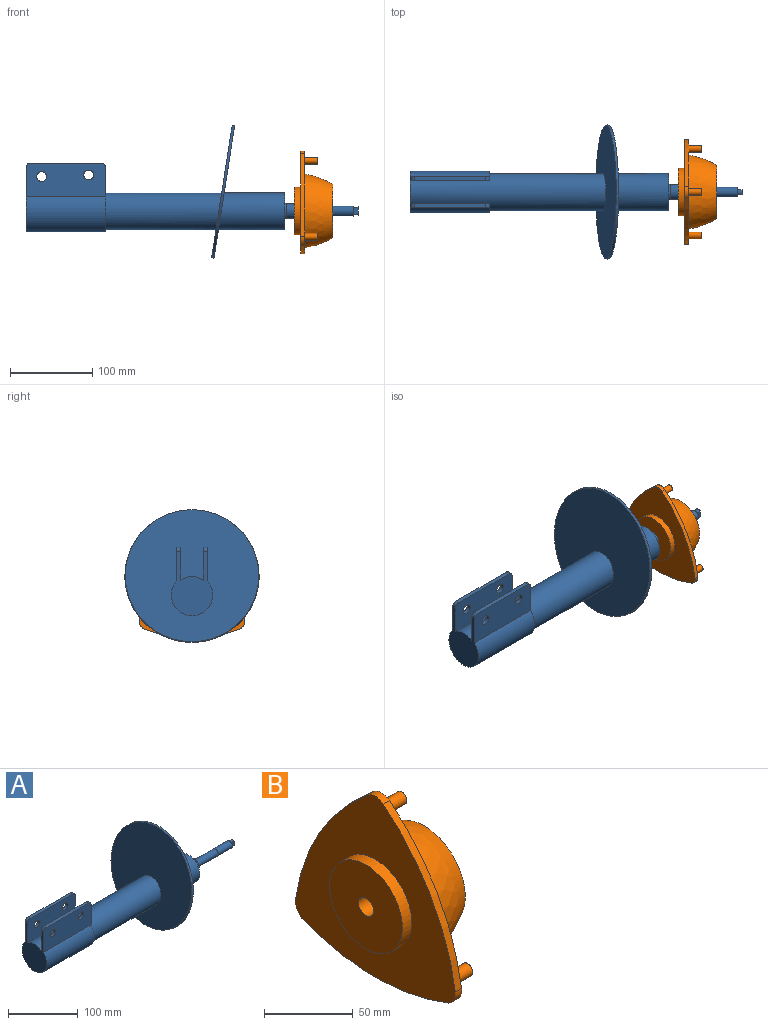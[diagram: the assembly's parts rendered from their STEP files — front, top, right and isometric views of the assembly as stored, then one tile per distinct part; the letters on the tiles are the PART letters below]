
ASSEMBLY  parts=2 mates=1
PART A: 41 faces, bbox 404x164.3x162.4 mm
  f0: plane 10x6mm, normal (1,0,0), area 56.2mm2, adj f1,f3,f12,f13
  f1: cylinder r=5mm len=6mm, axis (-1,0,0), area 38.6mm2, adj f0,f4,f12,f13
  f2: cylinder r=22.5mm len=80.19mm, axis (-1,0,0), area 10839.2mm2, adj f11,f15
  f3: cylinder r=5mm len=6mm, axis (-1,0,0), area 38.6mm2, adj f0,f4,f12,f13
  f4: plane 12x12mm, normal (1,0,0), area 56.9mm2, adj f1,f3,f5,f12,f13
  f5: cylinder r=6mm len=29mm, axis (-1,0,0), area 1093.3mm2, adj f4,f6
  f6: plane 12x12mm, normal (-1,0,0), area 3.7mm2, adj f5,f7
  f7: cylinder r=5.9mm len=42mm, axis (-1,0,0), area 1557mm2, adj f6,f8
  f8: plane 18x18mm, normal (1,0,0), area 145.1mm2, adj f7,f9
  f9: cylinder r=9mm len=18mm, axis (-1,0,0), area 565.5mm2, adj f8,f10
  f10: cone r=10mm half-angle=26.6deg, axis (-1,0,0), area 133.5mm2, adj f9,f11
  f11: plane 45x45mm, normal (1,0,0), area 1276.3mm2, adj f2,f10
  f12: plane 8x6mm, normal (0,1,0), area 48mm2, adj f0,f1,f3,f4
  f13: plane 8x6mm, normal (0,-1,0), area 48mm2, adj f0,f1,f3,f4
  f14: plane 161.94x160mm, normal (-0.99,0,0.15), area 18987.3mm2, adj f16,f26
  f15: plane 164.35x162.39mm, normal (0.99,0,-0.15), area 19223.6mm2, adj f2,f16
  f16: cone r=81.43mm half-angle=8.9deg, axis (0.99,0,-0.15), area 1530.6mm2, adj f14,f15
  f17: plane 86.5x5mm, normal (0,0,1), area 432.5mm2, adj f18,f24,f31,f32
  f18: plane 96.5x40.82mm, normal (0,1,0), area 3701.8mm2, adj f17,f19,f23,f25,f27,f28,f31,f32
  f19: cylinder r=25.25mm len=96.5mm, axis (-1,0,0), area 11302.8mm2, adj f18,f20,f23,f25
  f20: plane 96.5x40.82mm, normal (0,-1,0), area 3701.8mm2, adj f19,f21,f23,f25,f29,f30,f33,f34
  f21: plane 86.5x5mm, normal (0,0,1), area 432.5mm2, adj f20,f22,f33,f34
  f22: plane 96.5x40mm, normal (0,1,0), area 3623.1mm2, adj f21,f23,f25,f26,f29,f30,f33,f34
  f23: plane 78.25x50.5mm, normal (-1,0,0), area 2259.6mm2, adj f18,f19,f20,f22,f24,f26,f32,f34
  f24: plane 96.5x40mm, normal (0,-1,0), area 3623.1mm2, adj f17,f23,f25,f26,f27,f28,f31,f32
  f25: plane 78.25x50.5mm, normal (1,0,0), area 669.2mm2, adj f18,f19,f20,f22,f24,f26,f31,f33
  f26: cylinder r=22.5mm len=237.36mm, axis (-1,0,0), area 22208.7mm2, adj f14,f22,f23,f24,f25
  f27: cylinder r=6mm len=12mm, axis (0,-1,0), area 188.5mm2, adj f18,f24
  f28: cylinder r=6mm len=12mm, axis (0,-1,0), area 188.5mm2, adj f18,f24
  f29: cylinder r=6mm len=12mm, axis (0,-1,0), area 188.5mm2, adj f20,f22
  f30: cylinder r=6mm len=12mm, axis (0,-1,0), area 188.5mm2, adj f20,f22
  f31: cylinder r=5mm len=5mm, axis (0,1,0), area 39.3mm2, adj f17,f18,f24,f25
  f32: cylinder r=5mm len=5mm, axis (0,1,0), area 39.3mm2, adj f17,f18,f23,f24
  f33: cylinder r=5mm len=5mm, axis (0,1,0), area 39.3mm2, adj f20,f21,f22,f25
  f34: cylinder r=5mm len=5mm, axis (0,1,0), area 39.3mm2, adj f20,f21,f22,f23
  f35: plane 41x41mm, normal (-1,0,0), area 1320.3mm2, adj f36
  f36: cylinder r=20.5mm len=77.88mm, axis (-1,0,0), area 9618.1mm2, adj f35,f37
  f37: plane 42.35x42.35mm, normal (0.99,0,-0.15), area 1336.3mm2, adj f36
  f38: cylinder r=20.5mm len=235.03mm, axis (-1,0,0), area 29860.7mm2, adj f39,f40
  f39: plane 41x41mm, normal (1,0,0), area 1320.3mm2, adj f38
  f40: plane 42.35x42.35mm, normal (-0.99,0,0.15), area 1336.3mm2, adj f38
PART B: 19 faces, bbox 46.5x127.4x124.6 mm
  f0: plane 65x65mm, normal (1,0,0), area 3205.2mm2, adj f1,f6
  f1: revolved ~90x90mm, area 9080.5mm2, adj f0,f2
  f2: plane 127.41x124.63mm, normal (1,0,0), area 4430.2mm2, adj f1,f7,f8,f9,f10,f11,f12,f13
  f3: plane 127.41x124.63mm, normal (-1,0,0), area 8300.7mm2, adj f4,f7,f8,f9,f10,f11,f12
  f4: cylinder r=29mm len=58mm, axis (-1,0,0), area 1366.6mm2, adj f3,f5
  f5: plane 58x58mm, normal (-1,0,0), area 2529mm2, adj f4,f6
  f6: cylinder r=6mm len=46.5mm, axis (-1,0,0), area 1753mm2, adj f0,f5
  f7: cylinder r=158.67mm len=100.72mm, axis (1,0,0), area 593.2mm2, adj f2,f3,f11,f12
  f8: cylinder r=155.68mm len=114.78mm, axis (1,0,0), area 587.8mm2, adj f2,f3,f10,f11
  f9: cylinder r=158.65mm len=100.72mm, axis (1,0,0), area 593.2mm2, adj f2,f3,f10,f12
  f10: cylinder r=10mm len=10.73mm, axis (1,0,0), area 66.8mm2, adj f2,f3,f8,f9
  f11: cylinder r=10mm len=10.73mm, axis (1,0,0), area 66.8mm2, adj f2,f3,f7,f8
  f12: cylinder r=10mm len=12.57mm, axis (1,0,0), area 68mm2, adj f2,f3,f7,f9
  f13: cylinder r=4mm len=16mm, axis (-1,0,0), area 402.1mm2, adj f2,f14
  f14: plane 8x8mm, normal (1,0,0), area 50.3mm2, adj f13
  f15: cylinder r=4mm len=16mm, axis (-1,0,0), area 402.1mm2, adj f2,f16
  f16: plane 8x8mm, normal (1,0,0), area 50.3mm2, adj f15
  f17: cylinder r=4mm len=16mm, axis (-1,0,0), area 402.1mm2, adj f2,f18
  f18: plane 8x8mm, normal (1,0,0), area 50.3mm2, adj f17
PLACE A t=(17.68,-273.96,64.92)mm
PLACE B t=(343.18,-273.96,64.92)mm
MATE fastened A.f1 <-> B.f4  axis (1,0,0) through (343.18,-273.96,64.92)mm
